# Revit family: QF_ELECTROLUXPROFESSIONAL_1LSNTG_WS6-28_S
name_source: partatom
category: Attrezzature speciali
units: mm (PartAtom-declared; Revit-internal decimal feet)

## family parameters
Basato su piano di lavoro = No
Condiviso = No
Punto di calcolo locali = No
Quota connettore circolare = Usa diametro
Sempre verticale = Sì
Taglio con vuoti quando caricato = No
Tipo di parte = Normale

## types (1)
- 9867930224
    Cycle = 50 Hz
    Depth = 1030 mm  [stored 3.37927 ft]
    Depth Actual = 1030 mm  [stored 3.37927 ft]
    Descrizione = WASHER WS6-28 28KG STEAM 220-240/50/1N COMPASS PRO 6G01 ML 2xWATER POWDER+5xLIQ. VALV.OPEN SILVER 2.I/O DISCON. STOP
    Gas KW = 0
    Height = 1430.8 mm  [stored 4.69423 ft]
    Height Actual = 1430 mm  [stored 4.6916 ft]
    Item Number = 1LSPNB
    Latent Heat Output = 0.0
    Length Actual = 830 mm  [stored 2.7231 ft]
    Modello = WS6-28
    Phase = 1
    Produttore = Electrolux Professional
    Prospetto di default = 0 mm  [stored 0 ft]
    Sensible Heat Output = 0.0
    Steam Pounds per Hour = 0
    URL = www.electroluxprofessional.com
    Volts = 240 V
    Watts = 1100 W
    Weight = 262
    Width = 830 mm  [stored 2.7231 ft]

note: [stored X ft] marks values corroborated as IEEE doubles in the binary element streams (Revit-internal decimal feet)

## geometry (parser evidence)
native form markers: Sweep x4
no freeform markers — native parametric forms only
